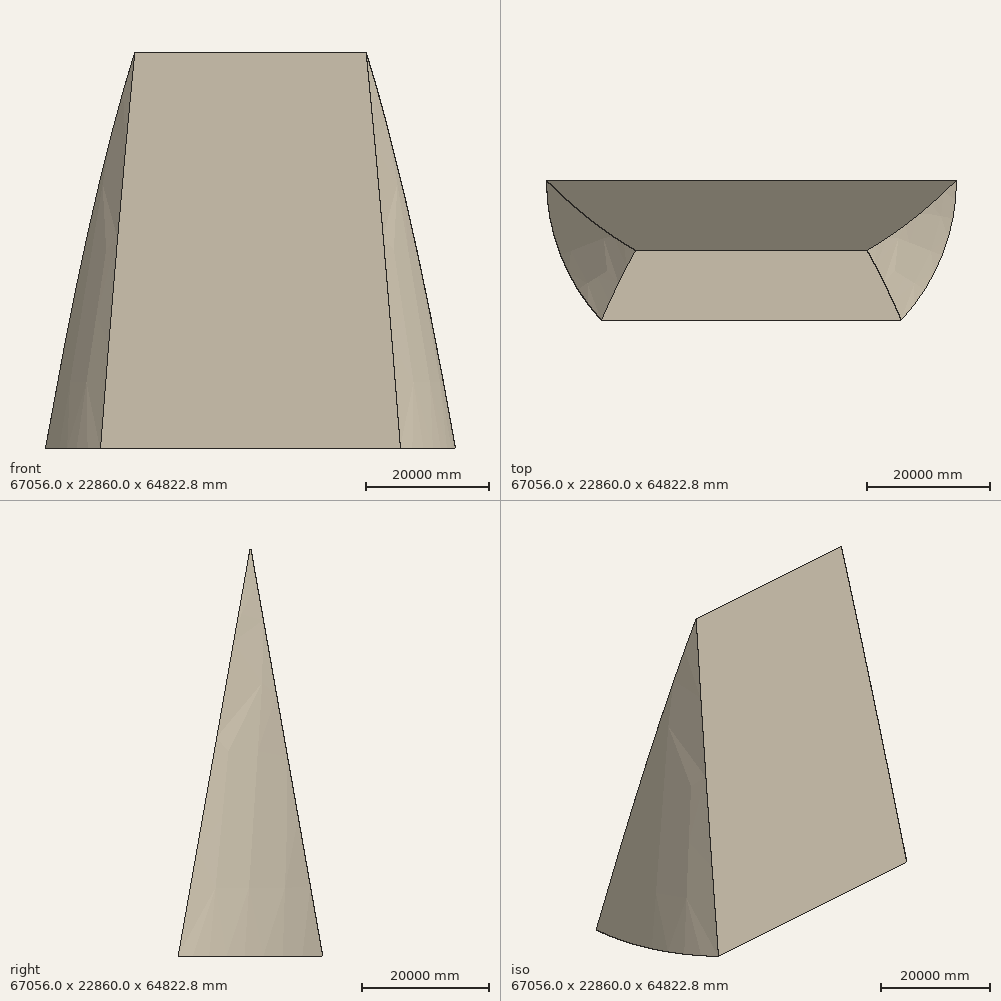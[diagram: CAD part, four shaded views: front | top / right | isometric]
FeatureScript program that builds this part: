
annotation { "Feature Type Name" : "Feature", "Feature Type Description" : "" }
export const myFeature = defineFeature(function(context is Context, id is Id, definition is map)
    precondition{}
    {
        {
            var Q0;
            Q0=qCreatedBy(makeId("Top.planeOp"),FACE);
            var sketch = newSketch(context, id + "F0", { "sketchPlane" : qUnion([Q0])});
            skCircle(sketch, "E0", {"center": v(0, 0) * mm, "radius": 33528 * mm});
            skLineSegment(sketch, "E1.bottom", {"start": v(35550.83, 0) * mm, "end": v(-35811.33, 0) * mm});
            skLineSegment(sketch, "E1.top", {"start": v(35550.83, -22860) * mm, "end": v(-35811.33, -22860) * mm});
            skLineSegment(sketch, "E1.left", {"start": v(35550.83, 0) * mm, "end": v(35550.83, -22860) * mm});
            skLineSegment(sketch, "E1.right", {"start": v(-35811.33, 0) * mm, "end": v(-35811.33, -22860) * mm});
            skSolve(sketch);
        }
        {
            var Q0;
            {var subQ0=sQuery(id+"F0.wireOp",EDGE,"E1.top");var subQ1=sQuery(id+"F0.wireOp",EDGE,"E0");var subQ2=makeQuery(id+"F0.imprint","INTERSECT",VERTEX,{"disambiguationData":[OD(0.0)],"derivedFrom":[subQ1,subQ0]});Q0=makeQuery(id+"F0.imprint","IMPRINT",FACE,{"disambiguationData":[TD([[makeQuery(id+"F0.imprint","IMPRINT",EDGE,{"disambiguationData":[TD([[subQ2,-1.0]])],"derivedFrom":subQ1}),1.0]])]});}
            var Q1;
            {var subQ0=sQuery(id+"F0.wireOp",EDGE,"E1.bottom");var subQ1=sQuery(id+"F0.wireOp",EDGE,"E0");var subQ2=makeQuery(id+"F0.imprint","INTERSECT",VERTEX,{"disambiguationData":[OD(0.0)],"derivedFrom":[subQ1,subQ0]});Q1=makeQuery(id+"F0.imprint","IMPRINT",FACE,{"disambiguationData":[TD([[makeQuery(id+"F0.imprint","IMPRINT",EDGE,{"disambiguationData":[TD([[subQ2,1.0]])],"derivedFrom":subQ1}),1.0]])]});}
            extrude(context, id + "F1", {"entities" : qUnion([Q0, Q1]), "depth" : 134112 * mm, "hasDraft" : true, "draftAngle" : 10 * degree, "draftPullDirection" : true});
        }
    });
